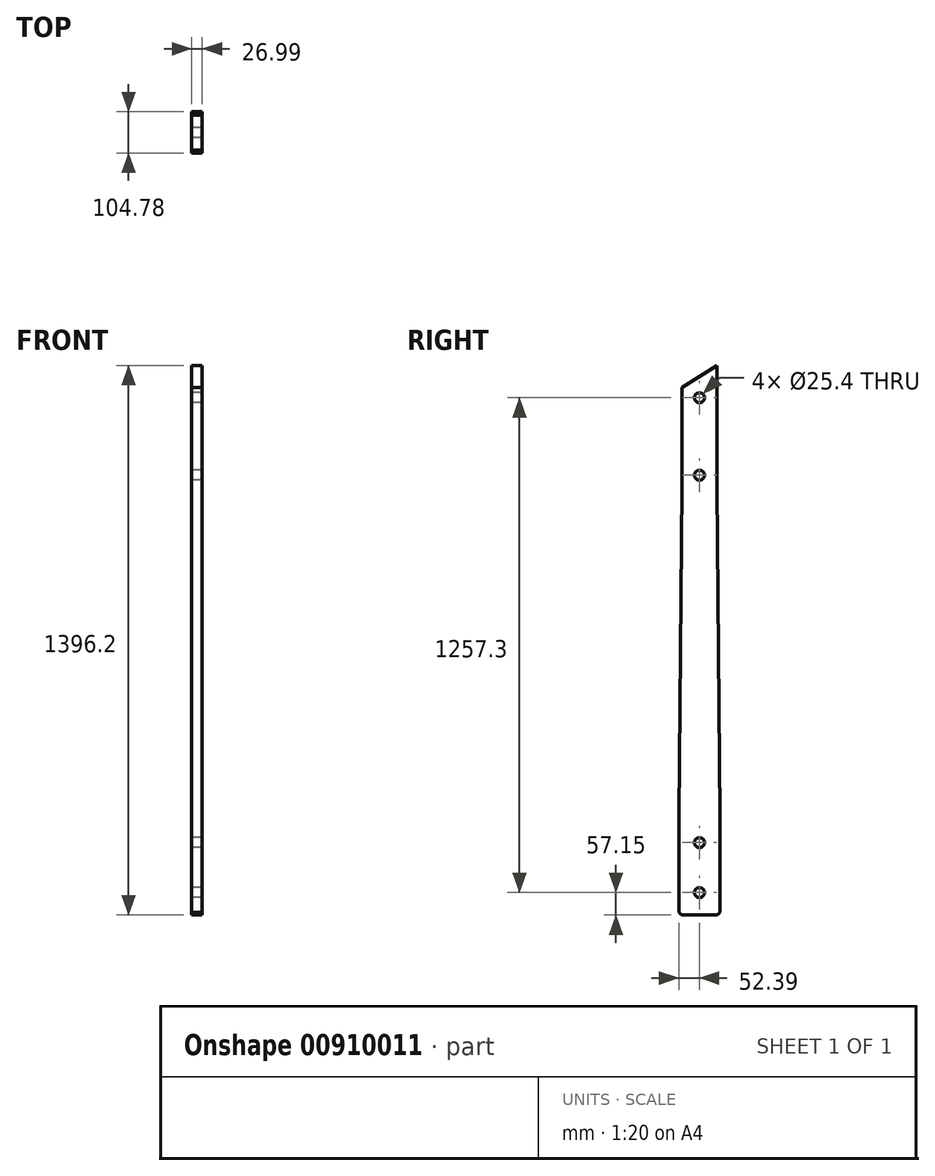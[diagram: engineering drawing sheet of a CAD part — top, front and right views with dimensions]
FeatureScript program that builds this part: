
annotation { "Feature Type Name" : "Feature", "Feature Type Description" : "" }
export const myFeature = defineFeature(function(context is Context, id is Id, definition is map)
    precondition{}
    {
        {
            var Q0;
            Q0=qCreatedBy(makeId("Right.planeOp"),FACE);
            var sketch = newSketch(context, id + "F0", { "sketchPlane" : qUnion([Q0])});
            skLineSegment(sketch, "E0", {"start": v(52.39, 0) * mm, "end": v(-52.39, 0) * mm});
            skLineSegment(sketch, "E1", {"start": v(-52.39, 0) * mm, "end": v(-52.39, 254) * mm});
            skLineSegment(sketch, "E2", {"start": v(-52.39, 254) * mm, "end": v(-44.45, 1085.85) * mm});
            skLineSegment(sketch, "E3", {"start": v(-44.45, 1085.85) * mm, "end": v(-44.45, 1340.65) * mm});
            skLineSegment(sketch, "E4", {"start": v(-44.45, 1340.65) * mm, "end": v(44.45, 1396.2) * mm});
            skLineSegment(sketch, "E5", {"start": v(44.45, 1396.2) * mm, "end": v(44.45, 1085.85) * mm});
            skLineSegment(sketch, "E6", {"start": v(44.45, 1085.85) * mm, "end": v(52.39, 254) * mm});
            skLineSegment(sketch, "E7", {"start": v(52.39, 254) * mm, "end": v(52.39, 0) * mm});
            skLineSegment(sketch, "E8", {"start": v(0, 1368.42) * mm, "end": v(0, 0) * mm, "construction": true});
            skCircle(sketch, "E9", {"center": v(0, 57.15) * mm, "radius": 12.7 * mm});
            skCircle(sketch, "E10", {"center": v(0, 184.15) * mm, "radius": 12.7 * mm});
            skCircle(sketch, "E11", {"center": v(0, 1117.6) * mm, "radius": 12.7 * mm});
            skCircle(sketch, "E12", {"center": v(0, 1314.45) * mm, "radius": 12.7 * mm});
            skSolve(sketch);
        }
        {
            var Q0;
            Q0=makeQuery(id+"F0.imprint","IMPRINT",FACE,{"disambiguationData":[TD([[makeQuery(id+"F0.imprint","IMPRINT",EDGE,{"derivedFrom":sQuery(id+"F0.wireOp",EDGE,"E0")}),-1.0]])]});
            extrude(context, id + "F1", {"entities" : qUnion([Q0]), "depth" : 26.99 * mm, "offsetDistance" : 25 * mm});
        }
        {
            var Q0;
            Q0=makeQuery(id+"F1.opExtrude","SWEPT_EDGE",EDGE,{"disambiguationData":[OSD([sQuery(id+"F0.wireOp",EDGE,"E0"),sQuery(id+"F0.wireOp",EDGE,"E1")])]});
            var Q1;
            Q1=makeQuery(id+"F1.opExtrude","SWEPT_EDGE",EDGE,{"disambiguationData":[OSD([sQuery(id+"F0.wireOp",EDGE,"E0"),sQuery(id+"F0.wireOp",EDGE,"E7")])]});
            chamfer(context, id + "F2", {"entities" : qUnion([Q0, Q1]), "width" : 6.35 * mm, "tangentPropagation" : true});
        }
    });
